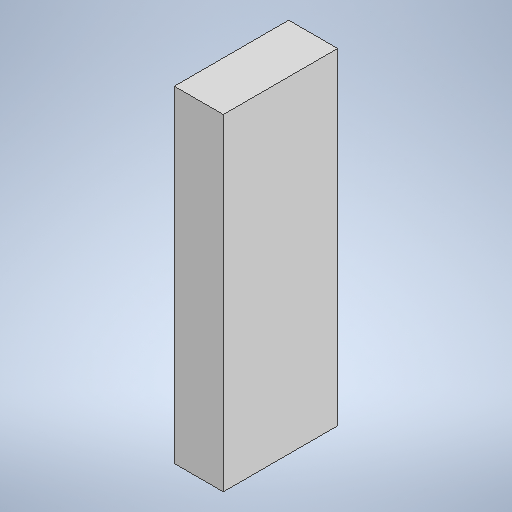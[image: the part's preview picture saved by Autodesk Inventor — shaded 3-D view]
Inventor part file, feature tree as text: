
AUTODESK INVENTOR PART (.ipt)
format: ipt  version: 2025 (Build 290162000, 162)  size: 252,928 bytes
history: native  units: in
note: dims shown in document units (in); Inventor stores cm internally (conversion verified against a paired STEP export)
features: extrude x1, sketch x1
ambient origin geometry x8: Origin, YZ Plane, XZ Plane, XY Plane, X Axis, Y Axis, Z Axis, Center Point
bodies: Solid1 (feature_tree)
feature tree (2):
  extrude  "Extrusion1"  Depth=3.5in
  sketch  "Sketch1"  dims[d0=10.0in d1=3.5in d2=1.5in d3=0.0in]
